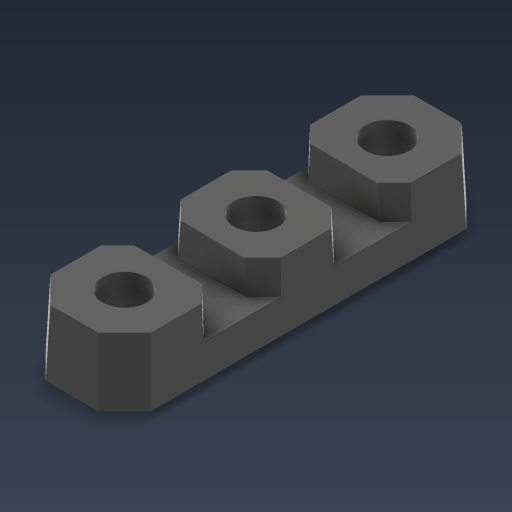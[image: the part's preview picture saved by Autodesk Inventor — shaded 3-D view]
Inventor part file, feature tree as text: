
AUTODESK INVENTOR PART (.ipt)
format: ipt  version: 2024.3 (Build 283343000, 343)  size: 415,232 bytes
history: native  units: in
note: dims shown in document units (in); Inventor stores cm internally (conversion verified against a paired STEP export)
features: projected_geometry x11, other x4, extrude x4, sketch x4, reference x2, imported_body x1
ambient origin geometry x8: Origin, YZ Plane, XZ Plane, XY Plane, X Axis, Y Axis, Z Axis, Center Point
bodies: Body1 (feature_tree)
feature tree (26):
  parser-record x1  (decoder bookkeeping rows leaked as tree rows — omitted from the tree; the rows remain in map.json)
  other  "BEARING-FLAT1"
  extrude  "Extrusion1"  Depth=1.0in TaperAngle=0.0deg
  extrude  "Extrusion2"  Depth=1.0in TaperAngle=0.0deg
  extrude  "Extrusion3"  [1 undecoded]
  extrude  "Extrusion4"  [1 undecoded]
  imported_body  "Base1"
  sketch  "Sketch2"  dims[d14=0.0in d15=0.0in d16=1.0in d17=0.0in]
  reference  "Reference1"
  reference  "Reference2"
  sketch  "Sketch3"  dims[d18=1.0in d19=0.0in d20=1.0in d21=0.0in]
  sketch  "Sketch4"
  projected_geometry  "Projected Loop1"
  projected_geometry  "Projected Loop3"
  projected_geometry  "Projected Loop4"
  projected_geometry  "Projected Loop5"
  projected_geometry  "Projected Loop6"
  projected_geometry  "Projected Loop7"
  projected_geometry  "Projected Loop8"
  sketch  "Sketch5"
  projected_geometry  "Projected Loop9"
  projected_geometry  "Projected Loop10"
  projected_geometry  "Projected Loop11"
  projected_geometry  "Projected Loop12"
  other  "Assembly1"
  other  "Alu C 1x2x1x5:1"
note: 2 required parameter values undecoded (feature->parameter linkage not recoverable at this tier; creation-order binding heuristic only, values carry confidence <= 0.55)
